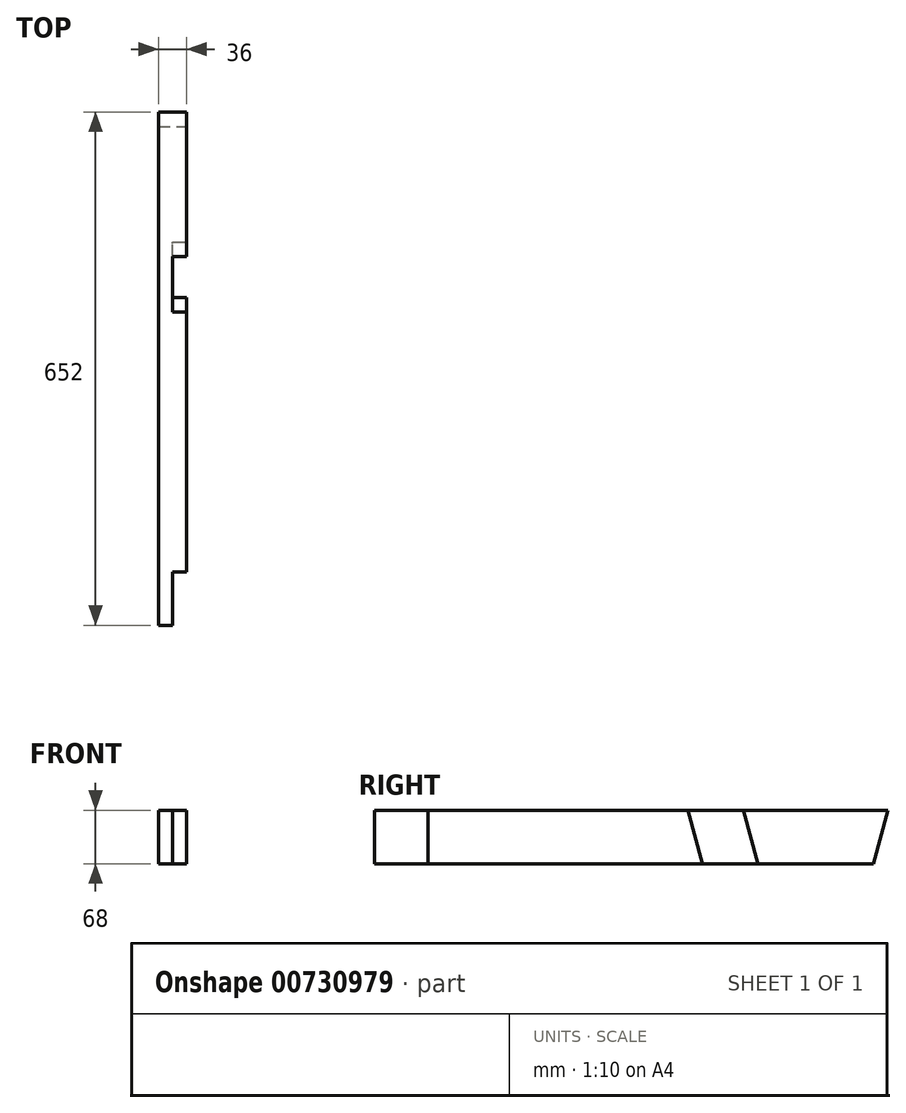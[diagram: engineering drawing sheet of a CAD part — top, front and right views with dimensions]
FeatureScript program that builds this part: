
annotation { "Feature Type Name" : "Feature", "Feature Type Description" : "" }
export const myFeature = defineFeature(function(context is Context, id is Id, definition is map)
    precondition{}
    {
        {
            var Q0;
            Q0=qCreatedBy(makeId("Front.planeOp"),FACE);
            var sketch = newSketch(context, id + "F0", { "sketchPlane" : qUnion([Q0])});
            skLineSegment(sketch, "E0.bottom", {"start": v(18, -34) * mm, "end": v(-18, -34) * mm});
            skLineSegment(sketch, "E0.top", {"start": v(18, 34) * mm, "end": v(-18, 34) * mm});
            skLineSegment(sketch, "E0.left", {"start": v(18, -34) * mm, "end": v(18, 34) * mm});
            skLineSegment(sketch, "E0.right", {"start": v(-18, -34) * mm, "end": v(-18, 34) * mm});
            skPoint(sketch, "E0.middle", {"position": v(0, 0) * mm});
            skSolve(sketch);
        }
        {
            var Q0;
            Q0 = qSketchRegion(id + "F0", true);
            extrude(context, id + "F1", {"entities" : qUnion([Q0]), "depth" : 652 * mm, "offsetDistance" : 25 * mm});
        }
        {
            var Q0;
            Q0=makeQuery(id+"F1.opExtrude","SWEPT_FACE",FACE,{"disambiguationData":[OSD([sQuery(id+"F0.wireOp",EDGE,"E0.left")])]});
            var sketch = newSketch(context, id + "F2", { "sketchPlane" : qUnion([Q0])});
            skLineSegment(sketch, "E1", {"start": v(0, 34) * mm, "end": v(-18.22, -34) * mm});
            skLineSegment(sketch, "E2", {"start": v(-18.22, -34) * mm, "end": v(0, -34) * mm});
            skLineSegment(sketch, "E3", {"start": v(0, -34) * mm, "end": v(0, 34) * mm});
            skSolve(sketch);
        }
        {
            var Q0;
            Q0=makeQuery(id+"F2.imprint","IMPRINT",FACE,{"disambiguationData":[TD([[makeQuery(id+"F2.imprint","IMPRINT",EDGE,{"derivedFrom":sQuery(id+"F2.wireOp",EDGE,"E1")}),1.0]])]});
            extrude(context, id + "F3", {"entities" : qUnion([Q0]), "operationType" : NewBodyOperationType.REMOVE, "endBound" : BoundingType.UP_TO_NEXT, "oppositeDirection" : true, "depth" : 25 * mm, "offsetDistance" : 25 * mm});
        }
        {
            var Q0;
            Q0=makeQuery(id+"F1.opExtrude","SWEPT_FACE",FACE,{"disambiguationData":[OSD([sQuery(id+"F0.wireOp",EDGE,"E0.left")])]});
            var sketch = newSketch(context, id + "F4", { "sketchPlane" : qUnion([Q0])});
            skLineSegment(sketch, "E4", {"start": v(-652, 34) * mm, "end": v(-584, 34) * mm});
            skLineSegment(sketch, "E5", {"start": v(-584, 34) * mm, "end": v(-584, -34) * mm});
            skLineSegment(sketch, "E6", {"start": v(-584, -34) * mm, "end": v(-652, -34) * mm});
            skLineSegment(sketch, "E7", {"start": v(-652, -34) * mm, "end": v(-652, 34) * mm});
            skSolve(sketch);
        }
        {
            var Q0;
            Q0=makeQuery(id+"F4.imprint","IMPRINT",FACE,{"disambiguationData":[TD([[makeQuery(id+"F4.imprint","IMPRINT",EDGE,{"derivedFrom":sQuery(id+"F4.wireOp",EDGE,"E4")}),-1.0]])]});
            extrude(context, id + "F5", {"entities" : qUnion([Q0]), "operationType" : NewBodyOperationType.REMOVE, "oppositeDirection" : true, "depth" : 18 * mm, "offsetDistance" : 25 * mm});
        }
        {
            var Q0;
            Q0=makeQuery(id+"F1.opExtrude","SWEPT_FACE",FACE,{"disambiguationData":[OSD([sQuery(id+"F0.wireOp",EDGE,"E0.left")])]});
            var sketch = newSketch(context, id + "F6", { "sketchPlane" : qUnion([Q0])});
            skLineSegment(sketch, "E8", {"start": v(-254, 34) * mm, "end": v(-183.5, 34) * mm});
            skLineSegment(sketch, "E9", {"start": v(-183.5, 34) * mm, "end": v(-165.28, -34) * mm});
            skLineSegment(sketch, "E10", {"start": v(-165.28, -34) * mm, "end": v(-235.78, -34) * mm});
            skLineSegment(sketch, "E11", {"start": v(-235.78, -34) * mm, "end": v(-254, 34) * mm});
            skSolve(sketch);
        }
        {
            var Q0;
            Q0=makeQuery(id+"F6.imprint","IMPRINT",FACE,{"disambiguationData":[TD([[makeQuery(id+"F6.imprint","IMPRINT",EDGE,{"derivedFrom":sQuery(id+"F6.wireOp",EDGE,"E8")}),-1.0]])]});
            extrude(context, id + "F7", {"entities" : qUnion([Q0]), "operationType" : NewBodyOperationType.REMOVE, "oppositeDirection" : true, "depth" : 18 * mm, "offsetDistance" : 25 * mm});
        }
    });
